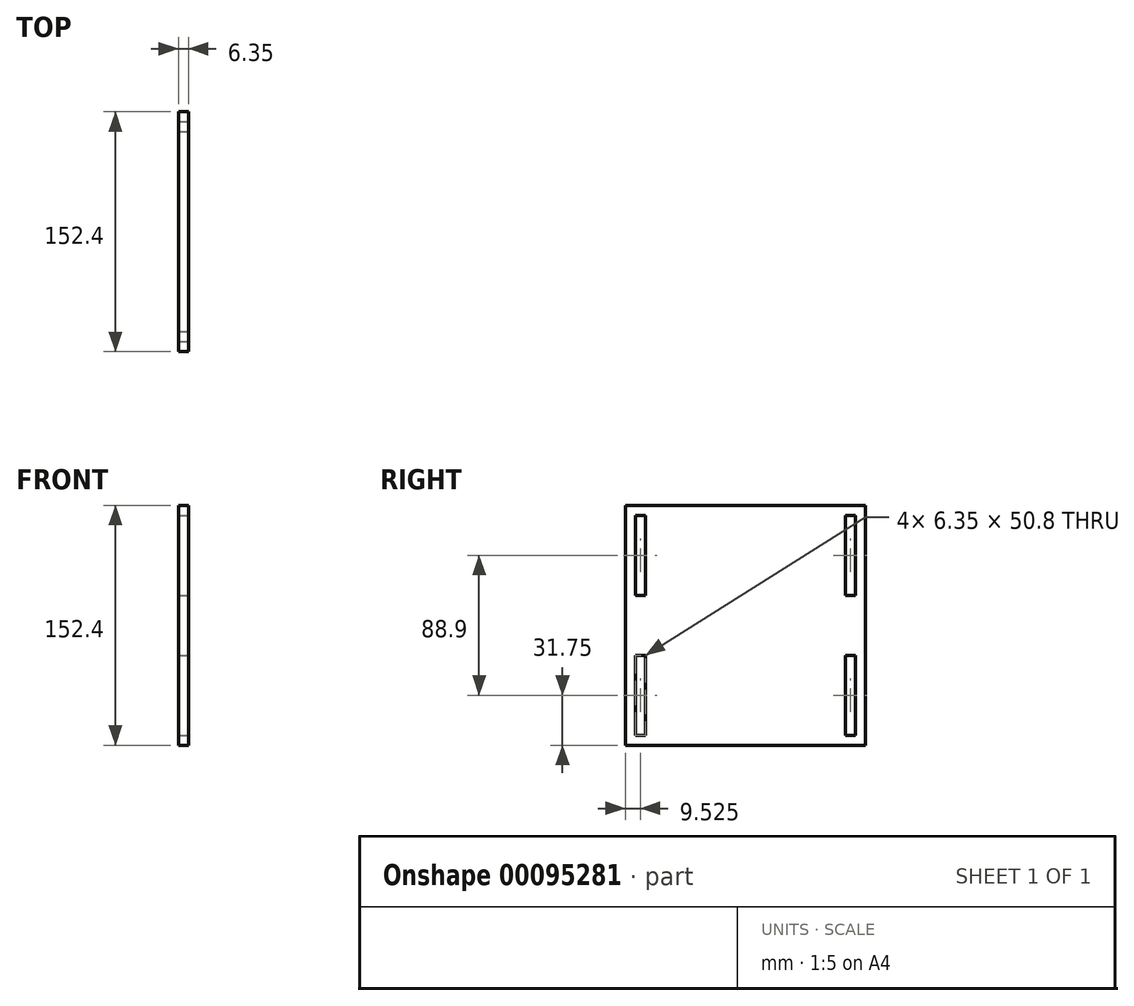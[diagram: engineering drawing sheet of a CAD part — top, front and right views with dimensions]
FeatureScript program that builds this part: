
annotation { "Feature Type Name" : "Feature", "Feature Type Description" : "" }
export const myFeature = defineFeature(function(context is Context, id is Id, definition is map)
    precondition{}
    {
        {
            var Q0;
            Q0=qCreatedBy(makeId("Right.planeOp"),FACE);
            var sketch = newSketch(context, id + "F0", { "sketchPlane" : qUnion([Q0])});
            skLineSegment(sketch, "E0.bottom", {"start": v(76.2, -76.2) * mm, "end": v(-76.2, -76.2) * mm});
            skLineSegment(sketch, "E0.top", {"start": v(76.2, 76.2) * mm, "end": v(-76.2, 76.2) * mm});
            skLineSegment(sketch, "E0.left", {"start": v(76.2, -76.2) * mm, "end": v(76.2, 76.2) * mm});
            skLineSegment(sketch, "E0.right", {"start": v(-76.2, -76.2) * mm, "end": v(-76.2, 76.2) * mm});
            skPoint(sketch, "E0.middle", {"position": v(0, 0) * mm});
            skSolve(sketch);
        }
        {
            var Q0;
            Q0 = qSketchRegion(id + "F0", true);
            extrude(context, id + "F1", {"entities" : qUnion([Q0]), "depth" : 6.35 * mm});
        }
        {
            var Q0;
            Q0=makeQuery(id+"F1.opExtrude","CAP_FACE",FACE,{"disambiguationData":[OSD([sQuery(id+"F0.wireOp",EDGE,"E0.bottom"),sQuery(id+"F0.wireOp",EDGE,"E0.top"),sQuery(id+"F0.wireOp",EDGE,"E0.left"),sQuery(id+"F0.wireOp",EDGE,"E0.right")])],"isStart":false});
            var sketch = newSketch(context, id + "F2", { "sketchPlane" : qUnion([Q0])});
            skLineSegment(sketch, "E1.bottom", {"start": v(-69.85, 69.85) * mm, "end": v(-63.5, 69.85) * mm});
            skLineSegment(sketch, "E1.top", {"start": v(-69.85, 19.05) * mm, "end": v(-63.5, 19.05) * mm});
            skLineSegment(sketch, "E1.left", {"start": v(-69.85, 69.85) * mm, "end": v(-69.85, 19.05) * mm});
            skLineSegment(sketch, "E1.right", {"start": v(-63.5, 69.85) * mm, "end": v(-63.5, 19.05) * mm});
            skLineSegment(sketch, "E2", {"start": v(0, -76.2) * mm, "end": v(0, 76.2) * mm, "construction": true});
            skLineSegment(sketch, "E3.MirrorCS", {"start": v(69.85, 69.85) * mm, "end": v(63.5, 69.85) * mm});
            skLineSegment(sketch, "E4.MirrorCS", {"start": v(69.85, 69.85) * mm, "end": v(69.85, 19.05) * mm});
            skLineSegment(sketch, "E5.MirrorCS", {"start": v(63.5, 69.85) * mm, "end": v(63.5, 19.05) * mm});
            skLineSegment(sketch, "E6.MirrorCS", {"start": v(69.85, 19.05) * mm, "end": v(63.5, 19.05) * mm});
            skLineSegment(sketch, "E7", {"start": v(-76.2, 0) * mm, "end": v(76.2, 0) * mm, "construction": true});
            skLineSegment(sketch, "E8.MirrorCS", {"start": v(-69.85, -19.05) * mm, "end": v(-63.5, -19.05) * mm});
            skLineSegment(sketch, "E9.MirrorCS", {"start": v(-63.5, -69.85) * mm, "end": v(-63.5, -19.05) * mm});
            skLineSegment(sketch, "E10.MirrorCS", {"start": v(-69.85, -69.85) * mm, "end": v(-69.85, -19.05) * mm});
            skLineSegment(sketch, "E11.MirrorCS", {"start": v(-69.85, -69.85) * mm, "end": v(-63.5, -69.85) * mm});
            skLineSegment(sketch, "E12.MirrorCS", {"start": v(63.5, -69.85) * mm, "end": v(63.5, -19.05) * mm});
            skLineSegment(sketch, "E13.MirrorCS", {"start": v(69.85, -19.05) * mm, "end": v(63.5, -19.05) * mm});
            skLineSegment(sketch, "E14.MirrorCS", {"start": v(69.85, -69.85) * mm, "end": v(69.85, -19.05) * mm});
            skLineSegment(sketch, "E15.MirrorCS", {"start": v(69.85, -69.85) * mm, "end": v(63.5, -69.85) * mm});
            skSolve(sketch);
        }
        {
            var Q0;
            Q0 = qSketchRegion(id + "F2", true);
            extrude(context, id + "F3", {"entities" : qUnion([Q0]), "operationType" : NewBodyOperationType.REMOVE, "oppositeDirection" : true, "depth" : 25.4 * mm});
        }
    });
